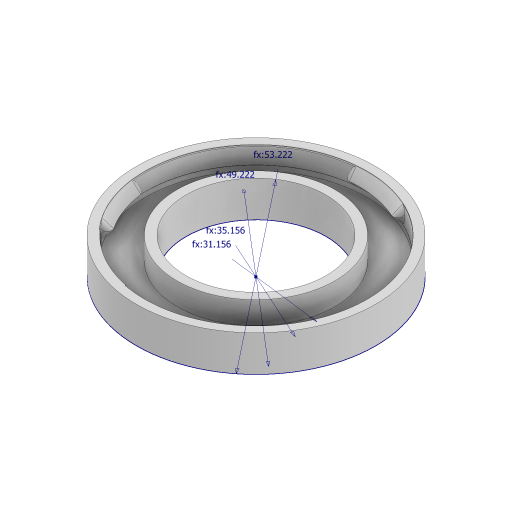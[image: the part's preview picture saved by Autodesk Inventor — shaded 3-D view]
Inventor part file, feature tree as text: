
AUTODESK INVENTOR PART (.ipt)
format: ipt  version: 2023 (Build 270158000, 158)  size: 402,432 bytes
history: native  units: mm
features: extrude x5, sketch x4, draft x2, revolve x1, fillet x1
ambient origin geometry x8: Origin, YZ Plane, XZ Plane, XY Plane, X Axis, Y Axis, Z Axis, Center Point
bodies: Solid1 (feature_tree)
feature tree (13):
  sketch  "Sketch1"  dims[d2=24.360984mm d3=24.031041mm]
  sketch  "Sketch2"  dims[d4=24.031041mm d6=31.156mm]
  extrude  "Extrusion1"  Depth=24.031041mm
  extrude  "Extrusion2"  Depth=31.156mm
  draft  "FaceDraft1"
  revolve  "Revolution2"  [1 undecoded]
  extrude  "Extrusion3"  Depth=35.156mm
  extrude  "Extrusion4"  Depth=49.221968mm
  extrude  "Extrusion5"  Depth=53.221968mm
  fillet  "Fillet2"  Radius=3.0mm
  draft  "FaceDraft2"
  sketch  "Sketch3"  dims[d7=17.828mm d8=17.828mm]
  sketch  "Sketch4"  dims[d9=17.828mm d10=35.156mm d11=49.221968mm d12=53.221968mm d13=3.0mm d14=0.0mm d15=8.0mm d16=0.0mm d17=0.261799mm d18=1.8mm d19=3.0mm d20=3.8mm d22=4.9mm d24=90.0deg d25=6.410091mm d30=5.934119mm d31=8.0mm d32=0.0mm d34=8.0mm d35=0.0mm d36=10.0mm d37=0.0mm d38=1.0mm d39=0.261799mm]
note: 1 required parameter value undecoded (feature->parameter linkage not recoverable at this tier; creation-order binding heuristic only, values carry confidence <= 0.55)
